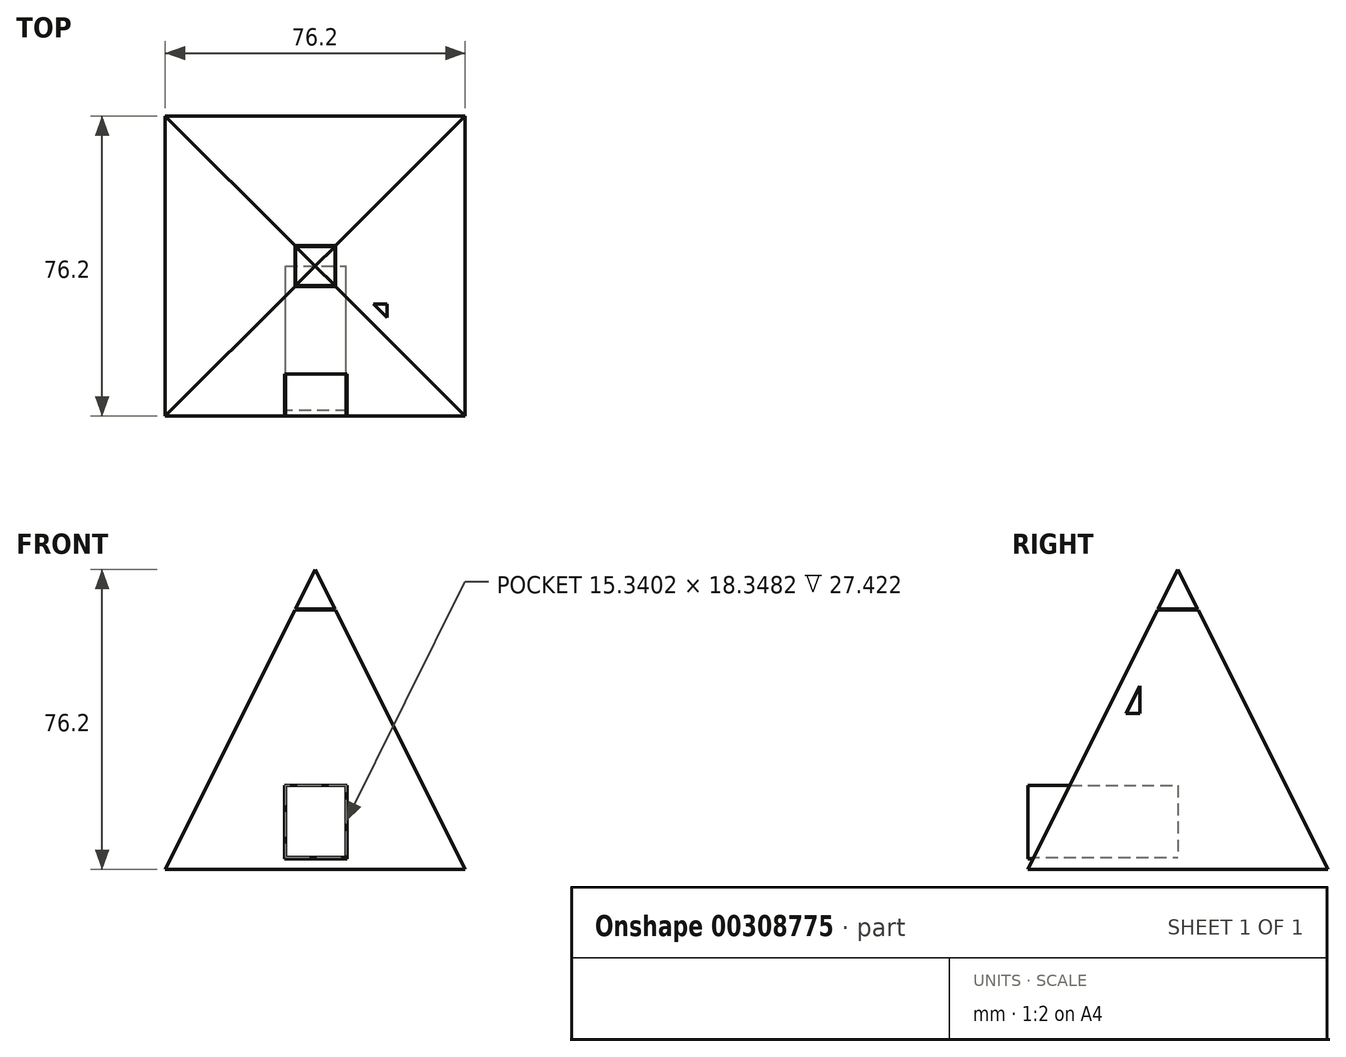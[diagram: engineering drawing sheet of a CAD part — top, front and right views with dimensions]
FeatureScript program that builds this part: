
annotation { "Feature Type Name" : "Feature", "Feature Type Description" : "" }
export const myFeature = defineFeature(function(context is Context, id is Id, definition is map)
    precondition{}
    {
        {
            var Q0;
            Q0=qCreatedBy(makeId("Front.planeOp"),FACE);
            var sketch = newSketch(context, id + "F0", { "sketchPlane" : qUnion([Q0])});
            skLineSegment(sketch, "E0.bottom", {"start": v(0, 0) * mm, "end": v(75.8, 0) * mm});
            skLineSegment(sketch, "E0.top", {"start": v(0, -76.1) * mm, "end": v(75.8, -76.1) * mm});
            skLineSegment(sketch, "E0.left", {"start": v(0, 0) * mm, "end": v(0, -76.1) * mm});
            skLineSegment(sketch, "E0.right", {"start": v(75.8, 0) * mm, "end": v(75.8, -76.1) * mm});
            skSolve(sketch);
        }
        {
            var Q0;
            Q0 = qSketchRegion(id + "F0", true);
            extrude(context, id + "F1", {"entities" : qUnion([Q0]), "depth" : 76.2 * mm});
        }
        {
            var Q0;
            Q0=makeQuery(id+"F1.opExtrude","CAP_FACE",FACE,{"disambiguationData":[OSD([sQuery(id+"F0.wireOp",EDGE,"E0.bottom"),sQuery(id+"F0.wireOp",EDGE,"E0.top"),sQuery(id+"F0.wireOp",EDGE,"E0.left"),sQuery(id+"F0.wireOp",EDGE,"E0.right")])],"isStart":false});
            var sketch = newSketch(context, id + "F2", { "sketchPlane" : qUnion([Q0])});
            skLineSegment(sketch, "E1.bottom", {"start": v(0, -76.1) * mm, "end": v(-94.86, -76.1) * mm});
            skLineSegment(sketch, "E1.top", {"start": v(0, -81.67) * mm, "end": v(-94.86, -81.67) * mm});
            skLineSegment(sketch, "E1.left", {"start": v(0, -76.1) * mm, "end": v(0, -81.67) * mm});
            skLineSegment(sketch, "E1.right", {"start": v(-94.86, -76.1) * mm, "end": v(-94.86, -81.67) * mm});
            skLineSegment(sketch, "E2", {"start": v(0, -76.1) * mm, "end": v(37.9, 0) * mm});
            skLineSegment(sketch, "E3", {"start": v(37.9, 0) * mm, "end": v(0, 0) * mm});
            skLineSegment(sketch, "E4", {"start": v(0, 0) * mm, "end": v(0, -76.1) * mm});
            skSolve(sketch);
        }
        {
            var Q0;
            Q0 = qSketchRegion(id + "F2", true);
            extrude(context, id + "F3", {"entities" : qUnion([Q0]), "operationType" : NewBodyOperationType.REMOVE, "oppositeDirection" : true, "depth" : 81.28 * mm});
        }
        {
            var Q0;
            Q0=makeQuery(id+"F1.opExtrude","CAP_FACE",FACE,{"disambiguationData":[OSD([sQuery(id+"F0.wireOp",EDGE,"E0.bottom"),sQuery(id+"F0.wireOp",EDGE,"E0.top"),sQuery(id+"F0.wireOp",EDGE,"E0.left"),sQuery(id+"F0.wireOp",EDGE,"E0.right")])],"isStart":false});
            var sketch = newSketch(context, id + "F4", { "sketchPlane" : qUnion([Q0])});
            skLineSegment(sketch, "E5", {"start": v(37.9, 0) * mm, "end": v(75.8, -76.1) * mm});
            skLineSegment(sketch, "E6", {"start": v(75.8, -76.1) * mm, "end": v(75.8, 0) * mm});
            skLineSegment(sketch, "E7", {"start": v(75.8, 0) * mm, "end": v(37.9, 0) * mm});
            skSolve(sketch);
        }
        {
            var Q0;
            Q0 = qSketchRegion(id + "F4", true);
            extrude(context, id + "F5", {"entities" : qUnion([Q0]), "operationType" : NewBodyOperationType.REMOVE, "oppositeDirection" : true, "depth" : 81.28 * mm});
        }
        {
            var Q0;
            Q0=makeQuery(id+"F1.opExtrude","SWEPT_BODY",BODY,{"disambiguationData":[OSD([sQuery(id+"F0.wireOp",EDGE,"E0.bottom"),sQuery(id+"F0.wireOp",EDGE,"E0.top"),sQuery(id+"F0.wireOp",EDGE,"E0.left"),sQuery(id+"F0.wireOp",EDGE,"E0.right")])]});
            deleteBodies(context, id + "F6", {"entities" : qUnion([Q0])});
        }
        {
            var Q0;
            Q0=qCreatedBy(makeId("Top.planeOp"),FACE);
            var sketch = newSketch(context, id + "F7", { "sketchPlane" : qUnion([Q0])});
            skLineSegment(sketch, "E8", {"start": v(0, 0) * mm, "end": v(0, 38.1) * mm});
            skLineSegment(sketch, "E9", {"start": v(0, 0) * mm, "end": v(38.1, 0) * mm});
            skLineSegment(sketch, "E10", {"start": v(0, 0) * mm, "end": v(-38.1, 0) * mm});
            skLineSegment(sketch, "E11", {"start": v(0, 0) * mm, "end": v(0, -38.1) * mm});
            skLineSegment(sketch, "E12", {"start": v(0, 38.1) * mm, "end": v(-38.1, 38.1) * mm});
            skLineSegment(sketch, "E13", {"start": v(-38.1, 38.1) * mm, "end": v(-38.1, -38.1) * mm});
            skLineSegment(sketch, "E14", {"start": v(-38.1, -38.1) * mm, "end": v(38.1, -38.1) * mm});
            skLineSegment(sketch, "E15", {"start": v(38.1, -38.1) * mm, "end": v(38.1, 38.1) * mm});
            skLineSegment(sketch, "E16", {"start": v(38.1, 38.1) * mm, "end": v(0, 38.1) * mm});
            skSolve(sketch);
        }
        {
            var Q0;
            Q0=qCreatedBy(makeId("Top.planeOp"),FACE);
            cPlane(context, id + "F8", {"entities" : qUnion([Q0]), "cplaneType" : CPlaneType.OFFSET, "offset" : 76.2 * mm, "width" : 152.4 * mm, "height" : 152.4 * mm});
        }
        {
            var Q0;
            Q0=qCreatedBy(id+"F8.planeOp",FACE);
            var sketch = newSketch(context, id + "F9", { "sketchPlane" : qUnion([Q0])});
            skPoint(sketch, "E17", {"position": v(0, 0) * mm});
            skSolve(sketch);
        }
        {
            var Q0;
            Q0=makeQuery(id+"F7.imprint","IMPRINT",FACE,{"disambiguationData":[TD([[makeQuery(id+"F7.imprint","IMPRINT",EDGE,{"derivedFrom":sQuery(id+"F7.wireOp",EDGE,"E8")}),1.0]])]});
            var Q1;
            Q1=sQuery(id+"F9.wireOp",VERTEX,"E17");
            loft(context, id + "F10", {"sheetProfilesArray" : [{ "sheetProfileEntities" : qUnion([Q0]) }, { "sheetProfileEntities" : qUnion([Q1]) }]});
        }
        {
            var Q1;
            {var subQ0=sQuery(id+"F7.wireOp",EDGE,"E10");Q1=makeQuery(id+"F7.imprint","IMPRINT",FACE,{"disambiguationData":[TD([[makeQuery(id+"F7.imprint","IMPRINT",EDGE,{"derivedFrom":subQ0}),1.0]])]});}
            var Q2;
            Q2=sQuery(id+"F9.wireOp",VERTEX,"E17");
            loft(context, id + "F11", {"operationType" : NewBodyOperationType.ADD, "sheetProfilesArray" : [{ "sheetProfileEntities" : qUnion([Q1]) }, { "sheetProfileEntities" : qUnion([Q2]) }]});
        }
        {
            var Q1;
            {var subQ0=sQuery(id+"F7.wireOp",EDGE,"E9");Q1=makeQuery(id+"F7.imprint","IMPRINT",FACE,{"disambiguationData":[TD([[makeQuery(id+"F7.imprint","IMPRINT",EDGE,{"derivedFrom":subQ0}),-1.0]])]});}
            var Q2;
            Q2=sQuery(id+"F9.wireOp",VERTEX,"E17");
            loft(context, id + "F12", {"operationType" : NewBodyOperationType.ADD, "sheetProfilesArray" : [{ "sheetProfileEntities" : qUnion([Q1]) }, { "sheetProfileEntities" : qUnion([Q2]) }]});
        }
        {
            var Q1;
            Q1=makeQuery(id+"F7.imprint","IMPRINT",FACE,{"disambiguationData":[TD([[makeQuery(id+"F7.imprint","IMPRINT",EDGE,{"derivedFrom":sQuery(id+"F7.wireOp",EDGE,"E8")}),-1.0]])]});
            var Q2;
            Q2=sQuery(id+"F9.wireOp",VERTEX,"E17");
            loft(context, id + "F13", {"operationType" : NewBodyOperationType.ADD, "sheetProfilesArray" : [{ "sheetProfileEntities" : qUnion([Q1]) }, { "sheetProfileEntities" : qUnion([Q2]) }]});
        }
        {
            var Q0;
            Q0=qCreatedBy(makeId("Front.planeOp"),FACE);
            var sketch = newSketch(context, id + "F14", { "sketchPlane" : qUnion([Q0])});
            skLineSegment(sketch, "E18.bottom", {"start": v(-16.54, 66.17) * mm, "end": v(17.45, 66.17) * mm});
            skLineSegment(sketch, "E18.top", {"start": v(-16.54, 65.87) * mm, "end": v(17.45, 65.87) * mm});
            skLineSegment(sketch, "E18.left", {"start": v(-16.54, 66.17) * mm, "end": v(-16.54, 65.87) * mm});
            skLineSegment(sketch, "E18.right", {"start": v(17.45, 66.17) * mm, "end": v(17.45, 65.87) * mm});
            skSolve(sketch);
        }
        {
            var Q0;
            Q0 = qSketchRegion(id + "F14", true);
            extrude(context, id + "F15", {"entities" : qUnion([Q0]), "operationType" : NewBodyOperationType.REMOVE, "oppositeDirection" : true, "depth" : 254 * mm, "hasSecondDirection" : true, "secondDirectionOppositeDirection" : false, "secondDirectionDepth" : 127 * mm});
        }
        {
            var Q0;
            {var subQ2=sQuery(id+"F7.wireOp",EDGE,"E14");var subQ12=sQuery(id+"F7.wireOp",EDGE,"E15");var subQ13=sQuery(id+"F7.wireOp",EDGE,"E16");var subQ14=sQuery(id+"F7.wireOp",EDGE,"E9");Q0=makeQuery(id+"F15.boolean.opBoolean","SPLIT",FACE,{"disambiguationData":[TD([makeQuery(id+"F15.opExtrude","SWEPT_FACE",FACE,{"disambiguationData":[OSD([sQuery(id+"F14.wireOp",EDGE,"E18.top")])]})])],"derivedFrom":makeQuery(id+"F13.boolean.opBoolean","MERGE",FACE,{"derivedFrom":[makeQuery(id+"F12.opLoft","SWEPT_FACE",FACE,{"disambiguationData":[OSD([subQ14,subQ2,subQ12])]}),makeQuery(id+"F13.opLoft","SWEPT_FACE",FACE,{"disambiguationData":[OSD([subQ14,subQ12,subQ13])]})]})});}
            var sketch = newSketch(context, id + "F16", { "sketchPlane" : qUnion([Q0])});
            skLineSegment(sketch, "E19", {"start": v(-9.63, 35.09) * mm, "end": v(-13.13, 27.24) * mm});
            skLineSegment(sketch, "E20", {"start": v(-13.13, 27.24) * mm, "end": v(-9.63, 27.24) * mm});
            skLineSegment(sketch, "E21", {"start": v(-9.63, 27.24) * mm, "end": v(-9.63, 35.09) * mm});
            skSolve(sketch);
        }
        {
            var Q0;
            Q0 = qSketchRegion(id + "F16", true);
            extrude(context, id + "F17", {"entities" : qUnion([Q0]), "operationType" : NewBodyOperationType.REMOVE, "oppositeDirection" : true, "depth" : 0.05 * mm});
        }
        {
            var Q0;
            Q0=qCreatedBy(makeId("Top.planeOp"),FACE);
            var sketch = newSketch(context, id + "F18", { "sketchPlane" : qUnion([Q0])});
            skCircle(sketch, "E22", {"center": v(0, 0) * mm, "radius": 48.74 * mm});
            skSolve(sketch);
        }
        {
            var Q0;
            Q0=qCreatedBy(makeId("Front.planeOp"),FACE);
            var sketch = newSketch(context, id + "F19", { "sketchPlane" : qUnion([Q0])});
            skLineSegment(sketch, "E23.bottom", {"start": v(-7.82, 2.7) * mm, "end": v(8.12, 2.7) * mm});
            skLineSegment(sketch, "E23.top", {"start": v(-7.82, 21.36) * mm, "end": v(8.12, 21.36) * mm});
            skLineSegment(sketch, "E23.left", {"start": v(-7.82, 2.7) * mm, "end": v(-7.82, 21.36) * mm});
            skLineSegment(sketch, "E23.right", {"start": v(8.12, 2.7) * mm, "end": v(8.12, 21.36) * mm});
            skSolve(sketch);
        }
        {
            var Q0;
            Q0 = qSketchRegion(id + "F19", true);
            extrude(context, id + "F20", {"entities" : qUnion([Q0]), "operationType" : NewBodyOperationType.ADD, "depth" : 38.1 * mm});
        }
        {
            var Q0;
            Q0=qCreatedBy(makeId("Front.planeOp"),FACE);
            var sketch = newSketch(context, id + "F21", { "sketchPlane" : qUnion([Q0])});
            skLineSegment(sketch, "E24.bottom", {"start": v(-7.52, 21.36) * mm, "end": v(7.82, 21.36) * mm});
            skLineSegment(sketch, "E24.top", {"start": v(-7.52, 3) * mm, "end": v(7.82, 3) * mm});
            skLineSegment(sketch, "E24.left", {"start": v(-7.52, 21.36) * mm, "end": v(-7.52, 3) * mm});
            skLineSegment(sketch, "E24.right", {"start": v(7.82, 21.36) * mm, "end": v(7.82, 3) * mm});
            skSolve(sketch);
        }
        {
            var Q0;
            Q0 = qSketchRegion(id + "F21", true);
            extrude(context, id + "F22", {"entities" : qUnion([Q0]), "operationType" : NewBodyOperationType.REMOVE, "depth" : 101.6 * mm});
        }
    });
